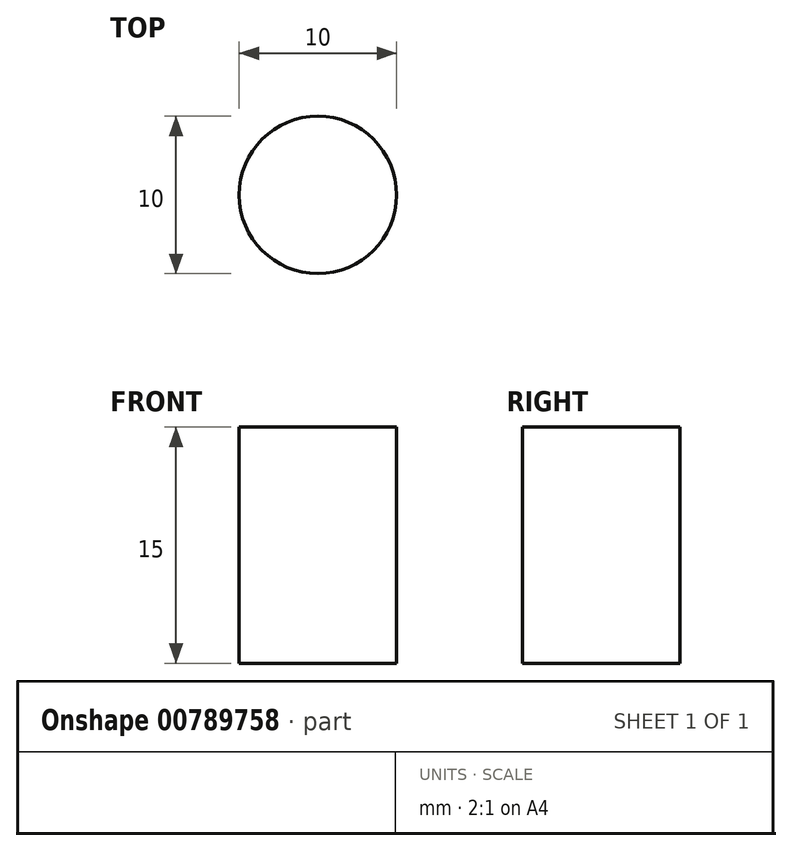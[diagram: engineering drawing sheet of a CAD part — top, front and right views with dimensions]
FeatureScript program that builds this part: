
annotation { "Feature Type Name" : "Feature", "Feature Type Description" : "" }
export const myFeature = defineFeature(function(context is Context, id is Id, definition is map)
    precondition{}
    {
        {
            var Q0;
            Q0=qCreatedBy(makeId("Top.planeOp"),FACE);
            var sketch = newSketch(context, id + "F0", { "sketchPlane" : qUnion([Q0])});
            skCircle(sketch, "E0", {"center": v(0, 0) * mm, "radius": 5 * mm});
            skSolve(sketch);
        }
        {
            var Q0;
            Q0=makeQuery(id+"F0.imprint","IMPRINT",FACE,{"disambiguationData":[TD([[makeQuery(id+"F0.imprint","IMPRINT",EDGE,{"derivedFrom":sQuery(id+"F0.wireOp",EDGE,"E0")}),1.0]])]});
            extrude(context, id + "F1", {"entities" : qUnion([Q0]), "depth" : 15 * mm, "offsetDistance" : 25 * mm});
        }
    });
